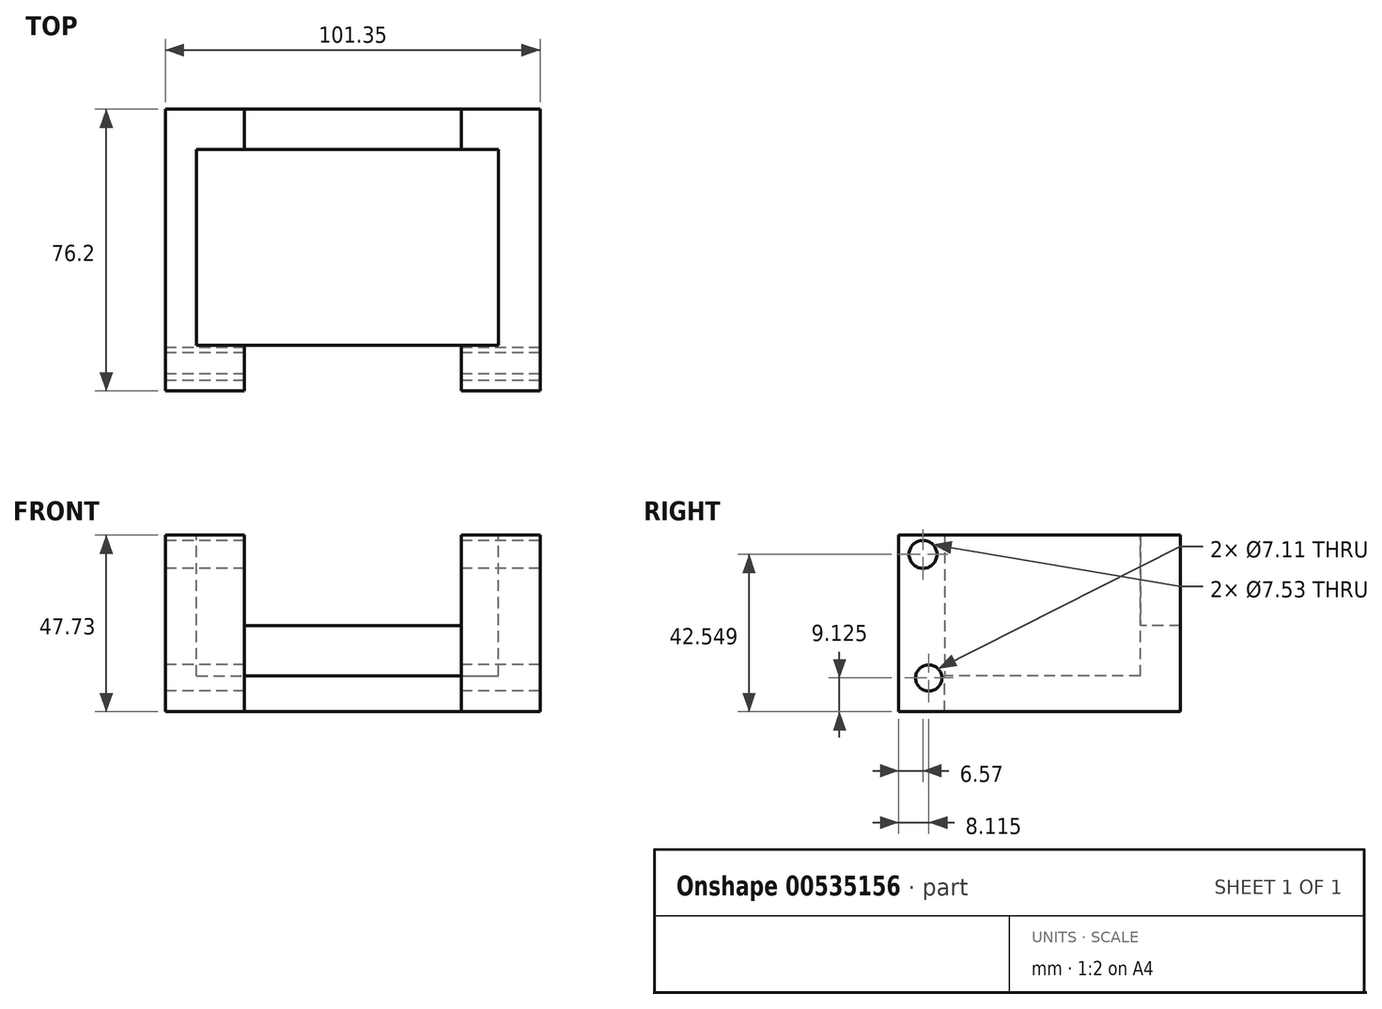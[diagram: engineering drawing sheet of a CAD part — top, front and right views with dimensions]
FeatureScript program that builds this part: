
annotation { "Feature Type Name" : "Feature", "Feature Type Description" : "" }
export const myFeature = defineFeature(function(context is Context, id is Id, definition is map)
    precondition{}
    {
        {
            var Q0;
            Q0=qCreatedBy(makeId("Front.planeOp"),FACE);
            var sketch = newSketch(context, id + "F0", { "sketchPlane" : qUnion([Q0])});
            skLineSegment(sketch, "E0.bottom", {"start": v(0, 0) * mm, "end": v(-101.35, 0) * mm});
            skLineSegment(sketch, "E0.top", {"start": v(0, 47.73) * mm, "end": v(-101.35, 47.73) * mm});
            skLineSegment(sketch, "E0.left", {"start": v(0, 0) * mm, "end": v(0, 47.73) * mm});
            skLineSegment(sketch, "E0.right", {"start": v(-101.35, 0) * mm, "end": v(-101.35, 47.73) * mm});
            skSolve(sketch);
        }
        {
            var Q0;
            Q0=makeQuery(id+"F0.imprint","IMPRINT",FACE,{"disambiguationData":[TD([[makeQuery(id+"F0.imprint","IMPRINT",EDGE,{"derivedFrom":sQuery(id+"F0.wireOp",EDGE,"E0.bottom")}),-1.0]])]});
            extrude(context, id + "F1", {"entities" : qUnion([Q0]), "depth" : 76.2 * mm});
        }
        {
            var Q0;
            Q0=makeQuery(id+"F1.opExtrude","SWEPT_FACE",FACE,{"disambiguationData":[OSD([sQuery(id+"F0.wireOp",EDGE,"E0.top")])]});
            var sketch = newSketch(context, id + "F2", { "sketchPlane" : qUnion([Q0])});
            skLineSegment(sketch, "E1.bottom", {"start": v(-92.9, -10.88) * mm, "end": v(-11.31, -10.88) * mm});
            skLineSegment(sketch, "E1.top", {"start": v(-92.9, -63.8) * mm, "end": v(-11.31, -63.8) * mm});
            skLineSegment(sketch, "E1.left", {"start": v(-92.9, -10.88) * mm, "end": v(-92.9, -63.8) * mm});
            skLineSegment(sketch, "E1.right", {"start": v(-11.31, -10.88) * mm, "end": v(-11.31, -63.8) * mm});
            skSolve(sketch);
        }
        {
            var Q0;
            Q0=makeQuery(id+"F2.imprint","IMPRINT",FACE,{"disambiguationData":[TD([[makeQuery(id+"F2.imprint","IMPRINT",EDGE,{"derivedFrom":sQuery(id+"F2.wireOp",EDGE,"E1.bottom")}),-1.0]])]});
            extrude(context, id + "F3", {"entities" : qUnion([Q0]), "operationType" : NewBodyOperationType.REMOVE, "oppositeDirection" : true, "depth" : 38.1 * mm});
        }
        {
            var Q0;
            Q0=makeQuery(id+"F1.opExtrude","CAP_FACE",FACE,{"disambiguationData":[OSD([sQuery(id+"F0.wireOp",EDGE,"E0.bottom"),sQuery(id+"F0.wireOp",EDGE,"E0.top"),sQuery(id+"F0.wireOp",EDGE,"E0.left"),sQuery(id+"F0.wireOp",EDGE,"E0.right")])],"isStart":false});
            var sketch = newSketch(context, id + "F4", { "sketchPlane" : qUnion([Q0])});
            skLineSegment(sketch, "E2.bottom", {"start": v(-79.95, 47.73) * mm, "end": v(-21.28, 47.73) * mm});
            skLineSegment(sketch, "E2.top", {"start": v(-79.95, 23.3) * mm, "end": v(-21.28, 23.3) * mm});
            skLineSegment(sketch, "E2.left", {"start": v(-79.95, 47.73) * mm, "end": v(-79.95, 23.3) * mm});
            skLineSegment(sketch, "E2.right", {"start": v(-21.28, 47.73) * mm, "end": v(-21.28, 23.3) * mm});
            skSolve(sketch);
        }
        {
            var Q0;
            Q0=makeQuery(id+"F4.imprint","IMPRINT",FACE,{"disambiguationData":[TD([[makeQuery(id+"F4.imprint","IMPRINT",EDGE,{"derivedFrom":sQuery(id+"F4.wireOp",EDGE,"E2.bottom")}),1.0]])]});
            extrude(context, id + "F5", {"entities" : qUnion([Q0]), "operationType" : NewBodyOperationType.REMOVE, "oppositeDirection" : true, "depth" : 76.2 * mm});
        }
        {
            var Q0;
            Q0=makeQuery(id+"F5.boolean.opBoolean","COPY",FACE,{"disambiguationData":[TD([makeQuery(id+"F3.boolean.opBoolean","COPY",FACE,{"derivedFrom":makeQuery(id+"F3.opExtrude","SWEPT_FACE",FACE,{"disambiguationData":[OSD([sQuery(id+"F2.wireOp",EDGE,"E1.top")])]})})])],"derivedFrom":makeQuery(id+"F5.opExtrude","SWEPT_FACE",FACE,{"disambiguationData":[OSD([sQuery(id+"F4.wireOp",EDGE,"E2.top")])]})});
            var sketch = newSketch(context, id + "F6", { "sketchPlane" : qUnion([Q0])});
            skLineSegment(sketch, "E3.bottom", {"start": v(-79.95, -63.8) * mm, "end": v(-21.28, -63.8) * mm});
            skLineSegment(sketch, "E3.top", {"start": v(-79.95, -76.2) * mm, "end": v(-21.28, -76.2) * mm});
            skLineSegment(sketch, "E3.left", {"start": v(-79.95, -63.8) * mm, "end": v(-79.95, -76.2) * mm});
            skLineSegment(sketch, "E3.right", {"start": v(-21.28, -63.8) * mm, "end": v(-21.28, -76.2) * mm});
            skSolve(sketch);
        }
        {
            var Q0;
            Q0=makeQuery(id+"F6.imprint","IMPRINT",FACE,{"disambiguationData":[TD([[makeQuery(id+"F6.imprint","IMPRINT",EDGE,{"derivedFrom":sQuery(id+"F6.wireOp",EDGE,"E3.bottom")}),-1.0]])]});
            extrude(context, id + "F7", {"entities" : qUnion([Q0]), "operationType" : NewBodyOperationType.REMOVE, "oppositeDirection" : true, "depth" : 50.8 * mm});
        }
        {
            var Q0;
            Q0=makeQuery(id+"F1.opExtrude","SWEPT_FACE",FACE,{"disambiguationData":[OSD([sQuery(id+"F0.wireOp",EDGE,"E0.right")])]});
            var sketch = newSketch(context, id + "F8", { "sketchPlane" : qUnion([Q0])});
            skCircle(sketch, "E4", {"center": v(68.09, 9.12) * mm, "radius": 3.55 * mm});
            skSolve(sketch);
        }
        {
            var Q0;
            Q0=makeQuery(id+"F8.imprint","IMPRINT",FACE,{"disambiguationData":[TD([[makeQuery(id+"F8.imprint","IMPRINT",EDGE,{"derivedFrom":sQuery(id+"F8.wireOp",EDGE,"E4")}),1.0]])]});
            extrude(context, id + "F9", {"entities" : qUnion([Q0]), "operationType" : NewBodyOperationType.REMOVE, "oppositeDirection" : true, "depth" : 127 * mm});
        }
        {
            var Q0;
            Q0=makeQuery(id+"F1.opExtrude","SWEPT_FACE",FACE,{"disambiguationData":[OSD([sQuery(id+"F0.wireOp",EDGE,"E0.right")])]});
            var sketch = newSketch(context, id + "F10", { "sketchPlane" : qUnion([Q0])});
            skCircle(sketch, "E5", {"center": v(69.63, 42.55) * mm, "radius": 3.77 * mm});
            skSolve(sketch);
        }
        {
            var Q0;
            Q0=makeQuery(id+"F10.imprint","IMPRINT",FACE,{"disambiguationData":[TD([[makeQuery(id+"F10.imprint","IMPRINT",EDGE,{"derivedFrom":sQuery(id+"F10.wireOp",EDGE,"E5")}),1.0]])]});
            extrude(context, id + "F11", {"entities" : qUnion([Q0]), "operationType" : NewBodyOperationType.REMOVE, "oppositeDirection" : true, "depth" : 127 * mm});
        }
    });
